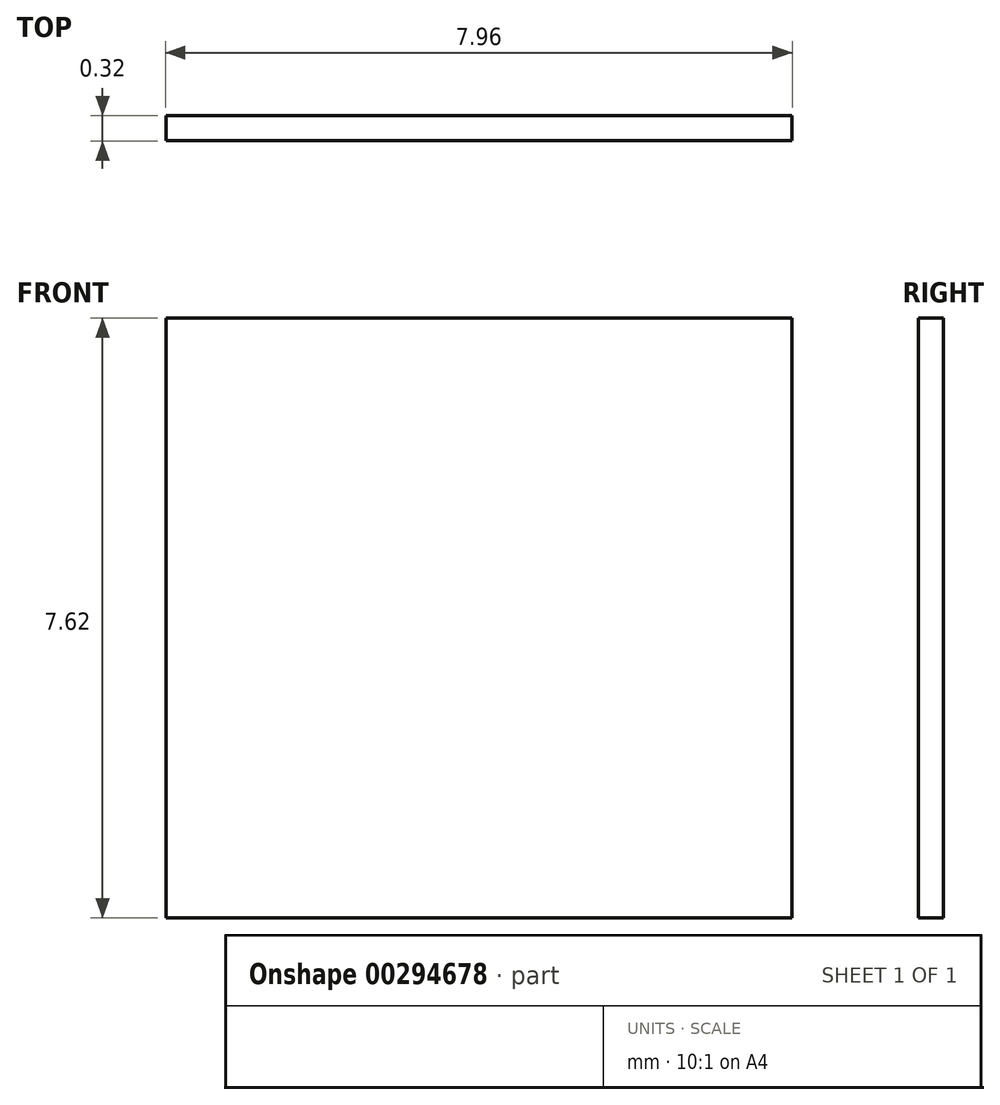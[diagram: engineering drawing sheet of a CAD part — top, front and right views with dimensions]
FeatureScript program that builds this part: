
annotation { "Feature Type Name" : "Feature", "Feature Type Description" : "" }
export const myFeature = defineFeature(function(context is Context, id is Id, definition is map)
    precondition{}
    {
        {
            var Q0;
            Q0=qCreatedBy(makeId("Front.planeOp"),FACE);
            var sketch = newSketch(context, id + "F0", { "sketchPlane" : qUnion([Q0])});
            skLineSegment(sketch, "E0.bottom", {"start": v(-3.98, 3.8) * mm, "end": v(3.98, 3.8) * mm});
            skLineSegment(sketch, "E0.top", {"start": v(-3.98, -3.81) * mm, "end": v(3.98, -3.81) * mm});
            skLineSegment(sketch, "E0.left", {"start": v(-3.98, 3.8) * mm, "end": v(-3.98, -3.81) * mm});
            skLineSegment(sketch, "E0.right", {"start": v(3.98, 3.8) * mm, "end": v(3.98, -3.81) * mm});
            skPoint(sketch, "E0.middle", {"position": v(0, 0) * mm});
            skSolve(sketch);
        }
        {
            var Q0;
            Q0 = qSketchRegion(id + "F0", true);
            extrude(context, id + "F1", {"entities" : qUnion([Q0]), "endBound" : BoundingType.SYMMETRIC, "depth" : 0.32 * mm});
        }
    });
